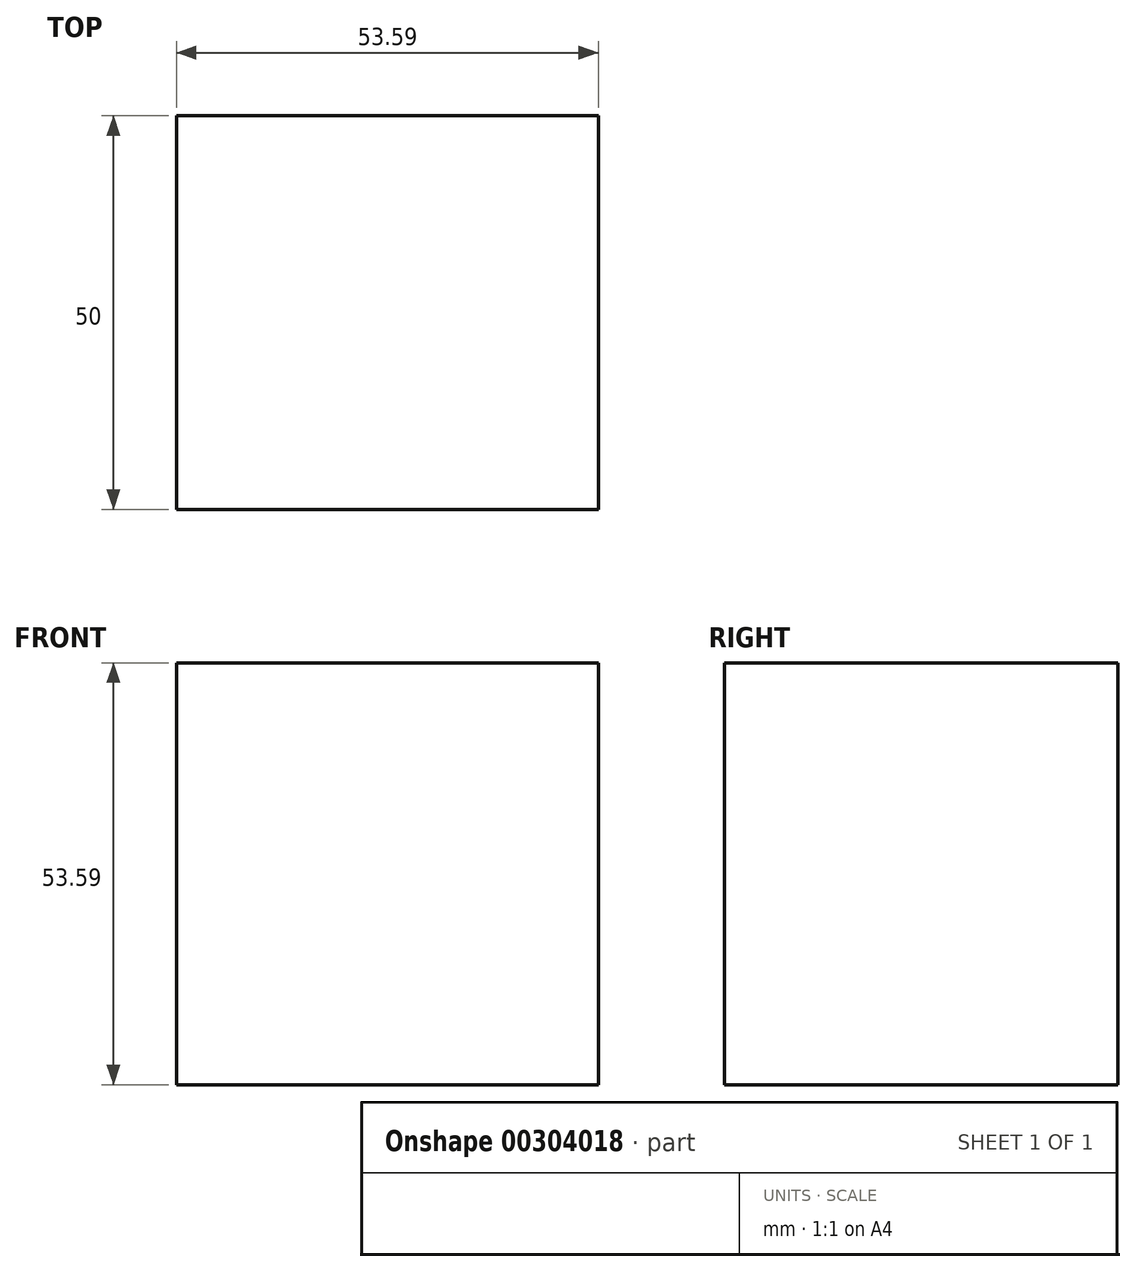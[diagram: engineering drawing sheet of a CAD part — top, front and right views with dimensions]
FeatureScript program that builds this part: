
annotation { "Feature Type Name" : "Feature", "Feature Type Description" : "" }
export const myFeature = defineFeature(function(context is Context, id is Id, definition is map)
    precondition{}
    {
        {
            var Q0;
            Q0=qCreatedBy(makeId("Front.planeOp"),FACE);
            var sketch = newSketch(context, id + "F0", { "sketchPlane" : qUnion([Q0])});
            skLineSegment(sketch, "E0.bottom", {"start": v(-16.32, 18.37) * mm, "end": v(37.27, 18.37) * mm});
            skLineSegment(sketch, "E0.top", {"start": v(-16.32, -35.22) * mm, "end": v(37.27, -35.22) * mm});
            skLineSegment(sketch, "E0.left", {"start": v(-16.32, 18.37) * mm, "end": v(-16.32, -35.22) * mm});
            skLineSegment(sketch, "E0.right", {"start": v(37.27, 18.37) * mm, "end": v(37.27, -35.22) * mm});
            skSolve(sketch);
        }
        {
            var Q0;
            Q0 = qSketchRegion(id + "F0", true);
            extrude(context, id + "F1", {"entities" : qUnion([Q0]), "depth" : 25 * mm, "hasSecondDirection" : true, "secondDirectionOppositeDirection" : true, "secondDirectionDepth" : 25 * mm});
        }
    });
